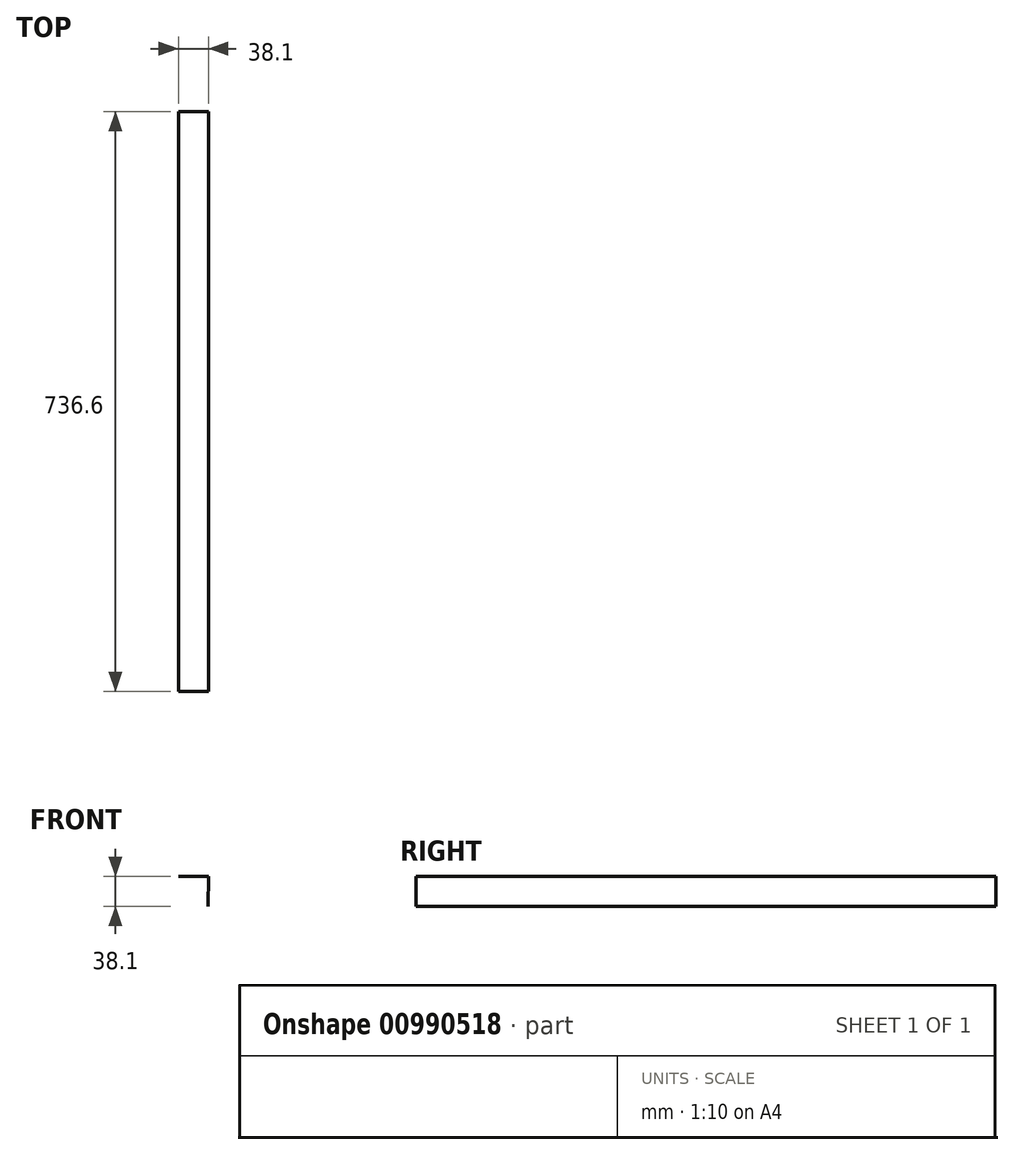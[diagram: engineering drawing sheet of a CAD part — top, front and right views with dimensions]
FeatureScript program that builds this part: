
annotation { "Feature Type Name" : "Feature", "Feature Type Description" : "" }
export const myFeature = defineFeature(function(context is Context, id is Id, definition is map)
    precondition{}
    {
        {
            var Q0;
            Q0=qCreatedBy(makeId("Front.planeOp"),FACE);
            var sketch = newSketch(context, id + "F0", { "sketchPlane" : qUnion([Q0])});
            skLineSegment(sketch, "E0", {"start": v(-171.44, 6.82) * mm, "end": v(-133.34, 6.82) * mm});
            skLineSegment(sketch, "E1", {"start": v(-133.34, 6.82) * mm, "end": v(-133.79, -31.28) * mm});
            skSolve(sketch);
        }
        {
            var Q0;
            Q0=sQuery(id+"F0.wireOp",EDGE,"E0");
            var Q1;
            Q1=sQuery(id+"F0.wireOp",EDGE,"E1");
            extrude(context, id + "F1", {"bodyType" : ToolBodyType.SURFACE, "surfaceEntities" : qUnion([Q0, Q1]), "depth" : 736.6 * mm, "offsetDistance" : 25.4 * mm});
        }
    });
